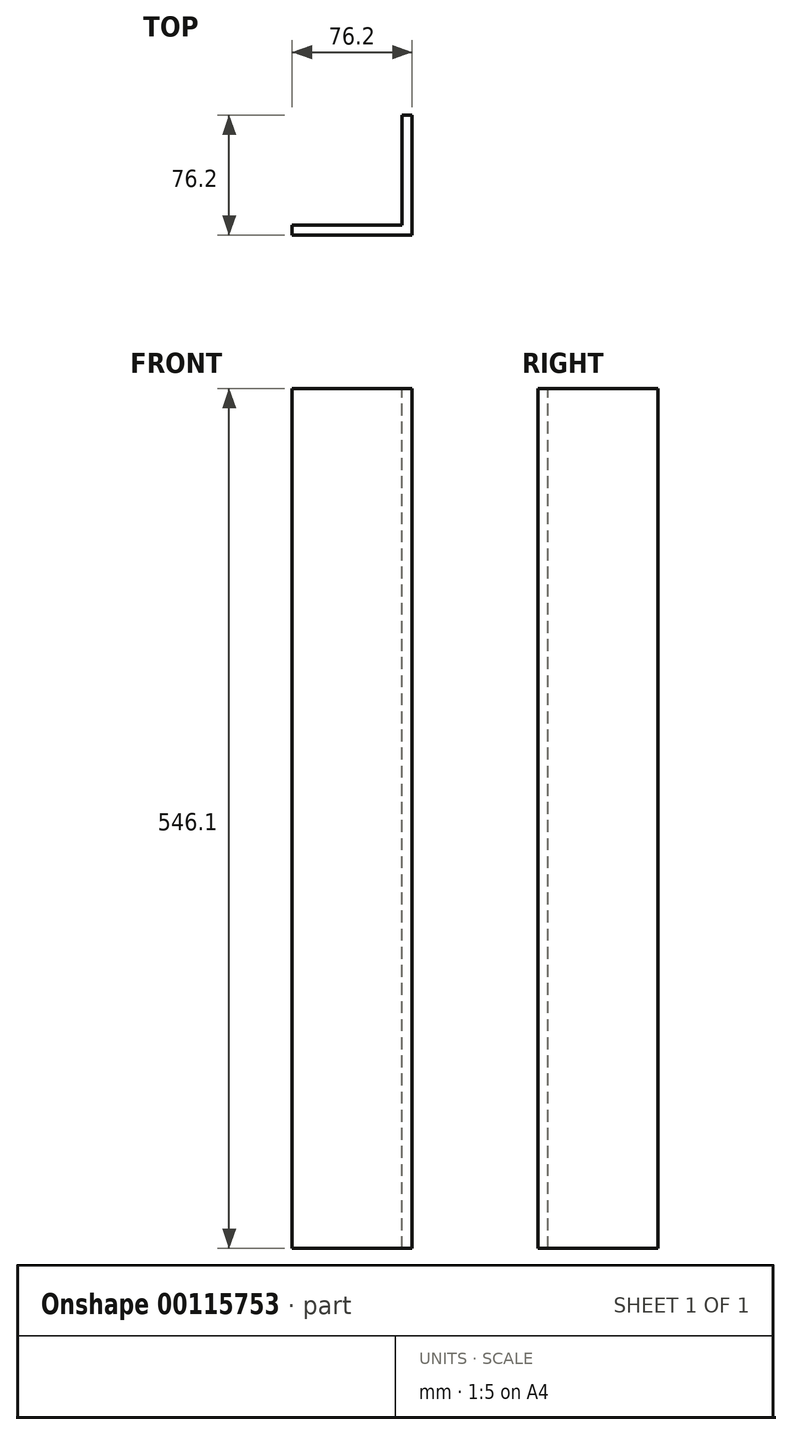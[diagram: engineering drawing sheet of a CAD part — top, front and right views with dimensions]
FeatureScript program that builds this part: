
annotation { "Feature Type Name" : "Feature", "Feature Type Description" : "" }
export const myFeature = defineFeature(function(context is Context, id is Id, definition is map)
    precondition{}
    {
        {
            var Q0;
            Q0=qCreatedBy(makeId("Top.planeOp"),FACE);
            var sketch = newSketch(context, id + "F0", { "sketchPlane" : qUnion([Q0])});
            skLineSegment(sketch, "E0", {"start": v(-76.2, 0) * mm, "end": v(0, 0) * mm});
            skLineSegment(sketch, "E1", {"start": v(0, 0) * mm, "end": v(0, 76.2) * mm});
            skLineSegment(sketch, "E2.0", {"start": v(-6.35, 6.35) * mm, "end": v(-6.35, 76.2) * mm});
            skLineSegment(sketch, "E2.1", {"start": v(-76.2, 6.35) * mm, "end": v(-6.35, 6.35) * mm});
            skLineSegment(sketch, "E3", {"start": v(-6.35, 76.2) * mm, "end": v(0, 76.2) * mm});
            skLineSegment(sketch, "E4", {"start": v(-76.2, 6.35) * mm, "end": v(-76.2, 0) * mm});
            skSolve(sketch);
        }
        {
            var Q0;
            Q0 = qSketchRegion(id + "F0", true);
            extrude(context, id + "F1", {"entities" : qUnion([Q0]), "oppositeDirection" : true, "depth" : 546.1 * mm});
        }
    });
